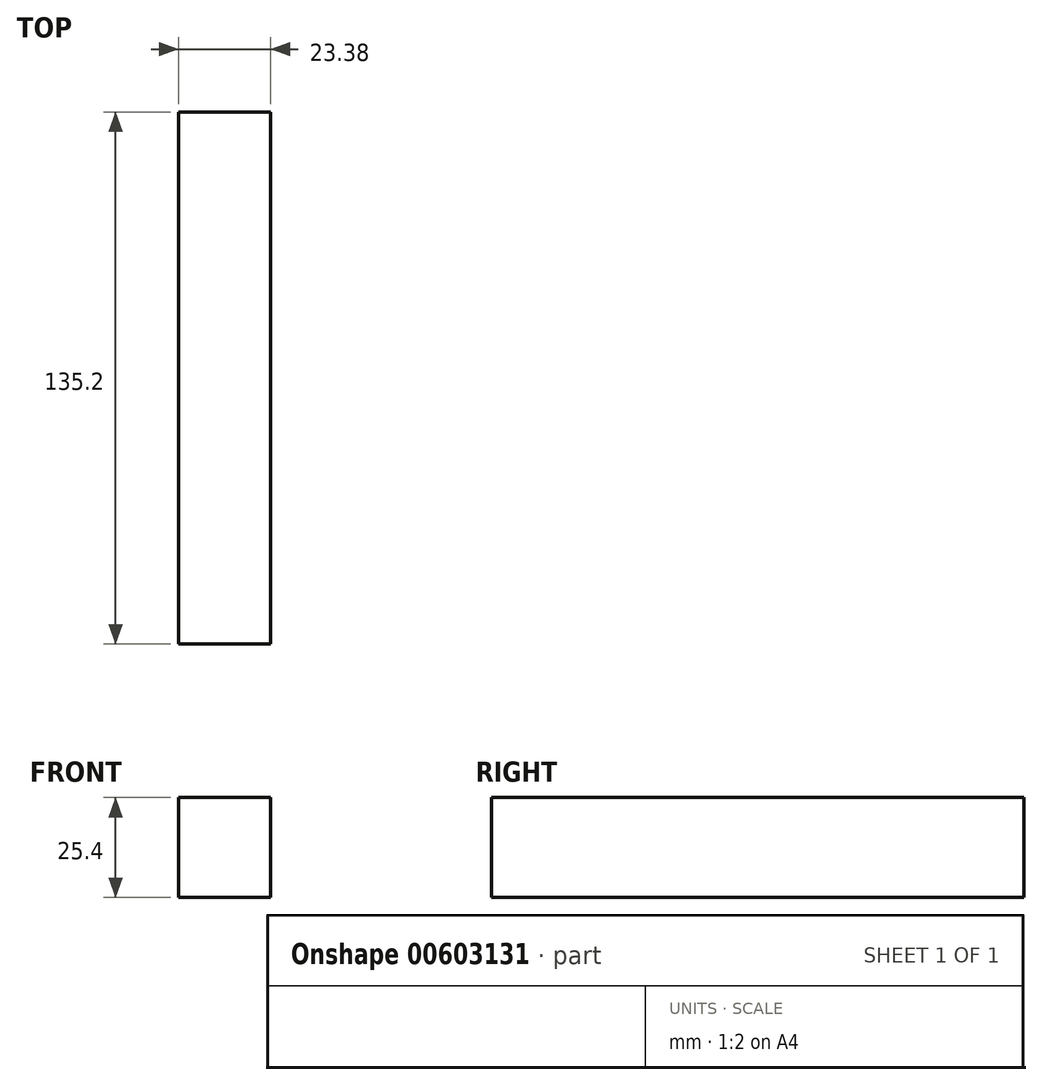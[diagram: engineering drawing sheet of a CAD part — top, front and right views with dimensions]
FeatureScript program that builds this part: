
annotation { "Feature Type Name" : "Feature", "Feature Type Description" : "" }
export const myFeature = defineFeature(function(context is Context, id is Id, definition is map)
    precondition{}
    {
        {
            var Q0;
            Q0=qCreatedBy(makeId("Top.planeOp"),FACE);
            var sketch = newSketch(context, id + "F0", { "sketchPlane" : qUnion([Q0])});
            skLineSegment(sketch, "E0.bottom", {"start": v(11.69, -67.6) * mm, "end": v(-11.69, -67.6) * mm});
            skLineSegment(sketch, "E0.top", {"start": v(11.69, 67.6) * mm, "end": v(-11.69, 67.6) * mm});
            skLineSegment(sketch, "E0.left", {"start": v(11.69, -67.6) * mm, "end": v(11.69, 67.6) * mm});
            skLineSegment(sketch, "E0.right", {"start": v(-11.69, -67.6) * mm, "end": v(-11.69, 67.6) * mm});
            skPoint(sketch, "E0.middle", {"position": v(0, 0) * mm});
            skSolve(sketch);
        }
        {
            var Q0;
            Q0 = qSketchRegion(id + "F0", true);
            extrude(context, id + "F1", {"entities" : qUnion([Q0]), "depth" : 25.4 * mm, "offsetDistance" : 25.4 * mm});
        }
    });
